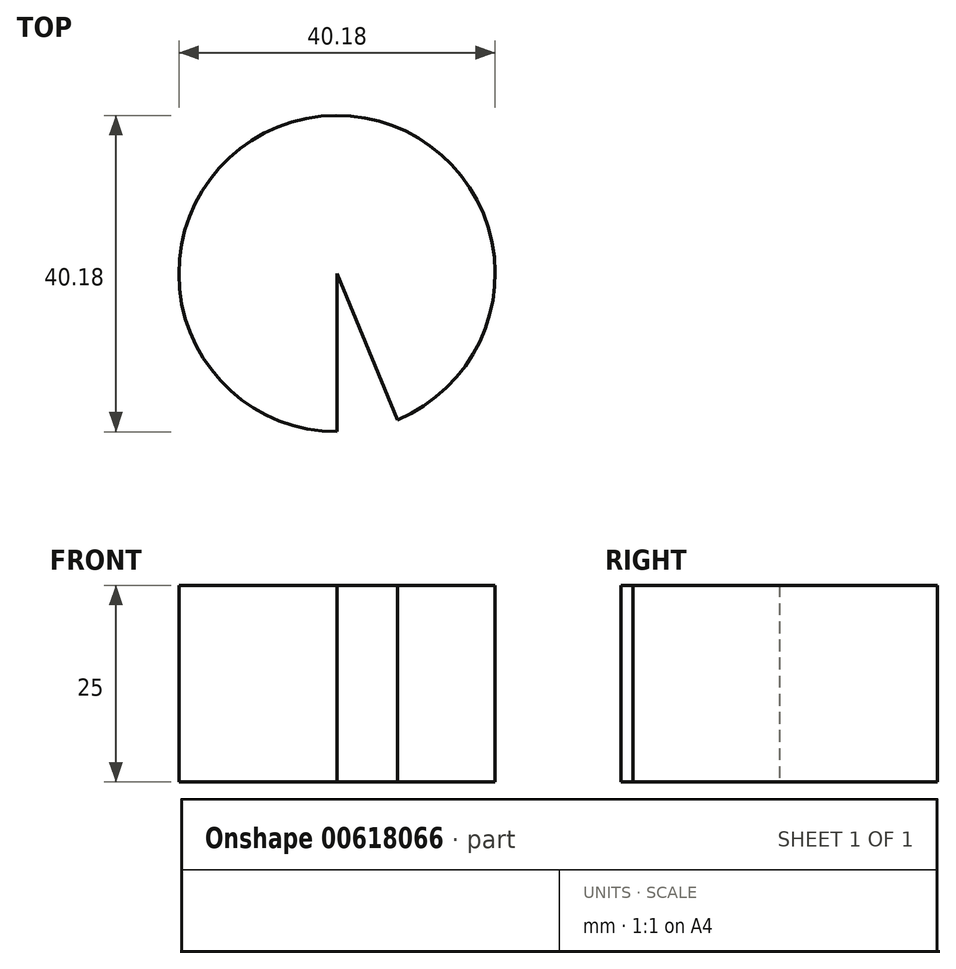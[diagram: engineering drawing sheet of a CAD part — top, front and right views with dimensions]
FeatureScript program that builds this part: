
annotation { "Feature Type Name" : "Feature", "Feature Type Description" : "" }
export const myFeature = defineFeature(function(context is Context, id is Id, definition is map)
    precondition{}
    {
        {
            var Q0;
            Q0=qCreatedBy(makeId("Top.planeOp"),FACE);
            var sketch = newSketch(context, id + "F0", { "sketchPlane" : qUnion([Q0])});
            skCircle(sketch, "E0", {"center": v(0, 0) * mm, "radius": 20.09 * mm});
            skLineSegment(sketch, "E1", {"start": v(0, 0) * mm, "end": v(0, -20.09) * mm});
            skLineSegment(sketch, "E2", {"start": v(0, -20.09) * mm, "end": v(7.66, -18.57) * mm});
            skLineSegment(sketch, "E3", {"start": v(7.66, -18.57) * mm, "end": v(0, 0) * mm});
            skSolve(sketch);
        }
        {
            var Q0;
            {var subQ1=sQuery(id+"F0.wireOp",EDGE,"E1");Q0=makeQuery(id+"F0.imprint","IMPRINT",FACE,{"disambiguationData":[TD([[makeQuery(id+"F0.imprint","IMPRINT",EDGE,{"derivedFrom":subQ1}),-1.0]])]});}
            extrude(context, id + "F1", {"entities" : qUnion([Q0]), "depth" : 25 * mm, "offsetDistance" : 25 * mm});
        }
    });
